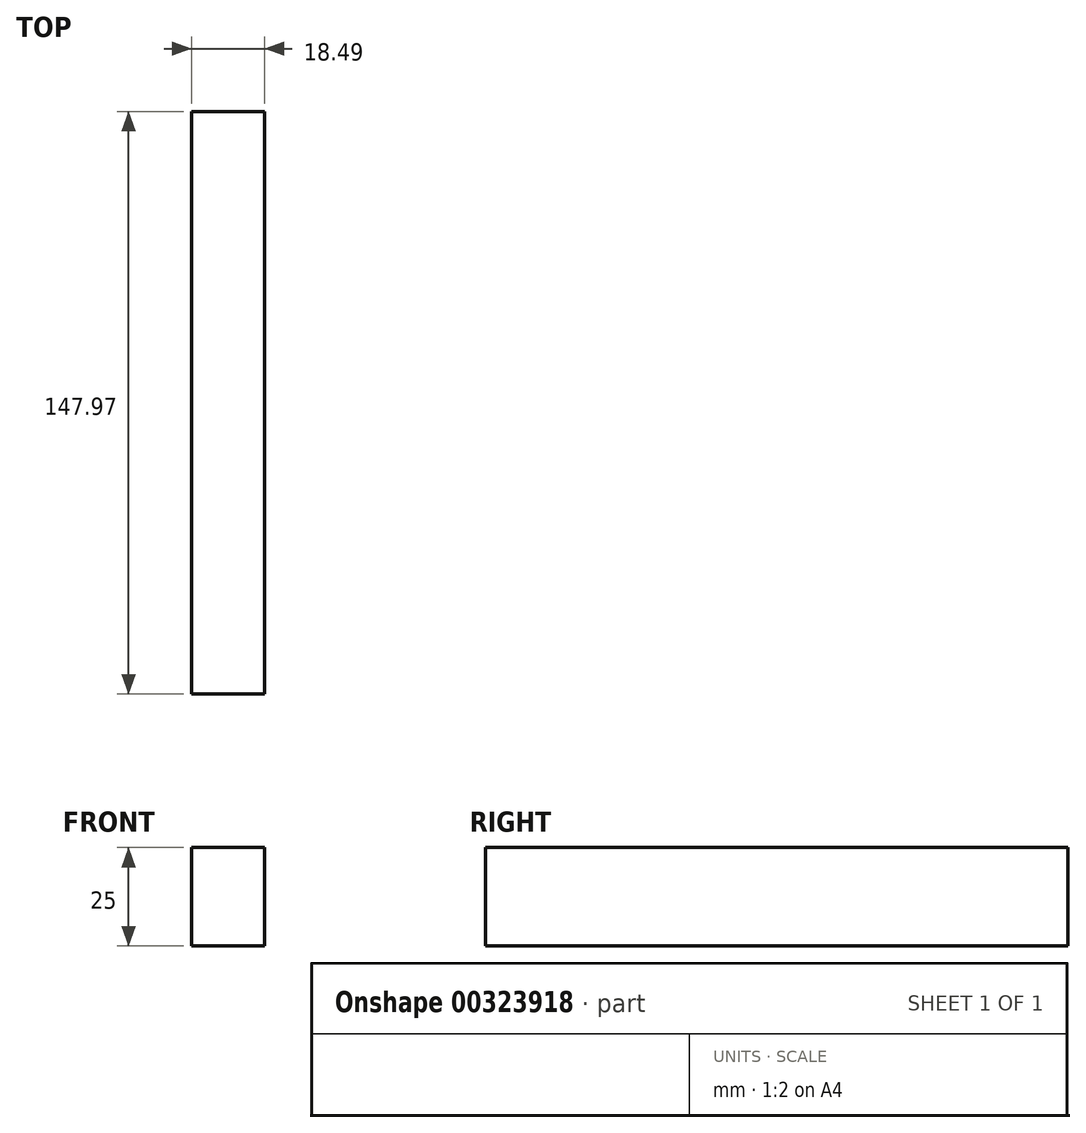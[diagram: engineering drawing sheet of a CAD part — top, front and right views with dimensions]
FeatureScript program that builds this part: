
annotation { "Feature Type Name" : "Feature", "Feature Type Description" : "" }
export const myFeature = defineFeature(function(context is Context, id is Id, definition is map)
    precondition{}
    {
        {
            var Q0;
            Q0=qCreatedBy(makeId("Top.planeOp"),FACE);
            var sketch = newSketch(context, id + "F0", { "sketchPlane" : qUnion([Q0])});
            skLineSegment(sketch, "E0.bottom", {"start": v(-18.5, 73.86) * mm, "end": v(0, 73.86) * mm});
            skLineSegment(sketch, "E0.top", {"start": v(-18.5, -74.11) * mm, "end": v(0, -74.11) * mm});
            skLineSegment(sketch, "E0.left", {"start": v(-18.5, 73.86) * mm, "end": v(-18.5, -74.11) * mm});
            skLineSegment(sketch, "E0.right", {"start": v(0, 73.86) * mm, "end": v(0, -74.11) * mm});
            skSolve(sketch);
        }
        {
            var Q0;
            Q0 = qSketchRegion(id + "F0", true);
            extrude(context, id + "F1", {"entities" : qUnion([Q0]), "depth" : 25 * mm});
        }
    });
